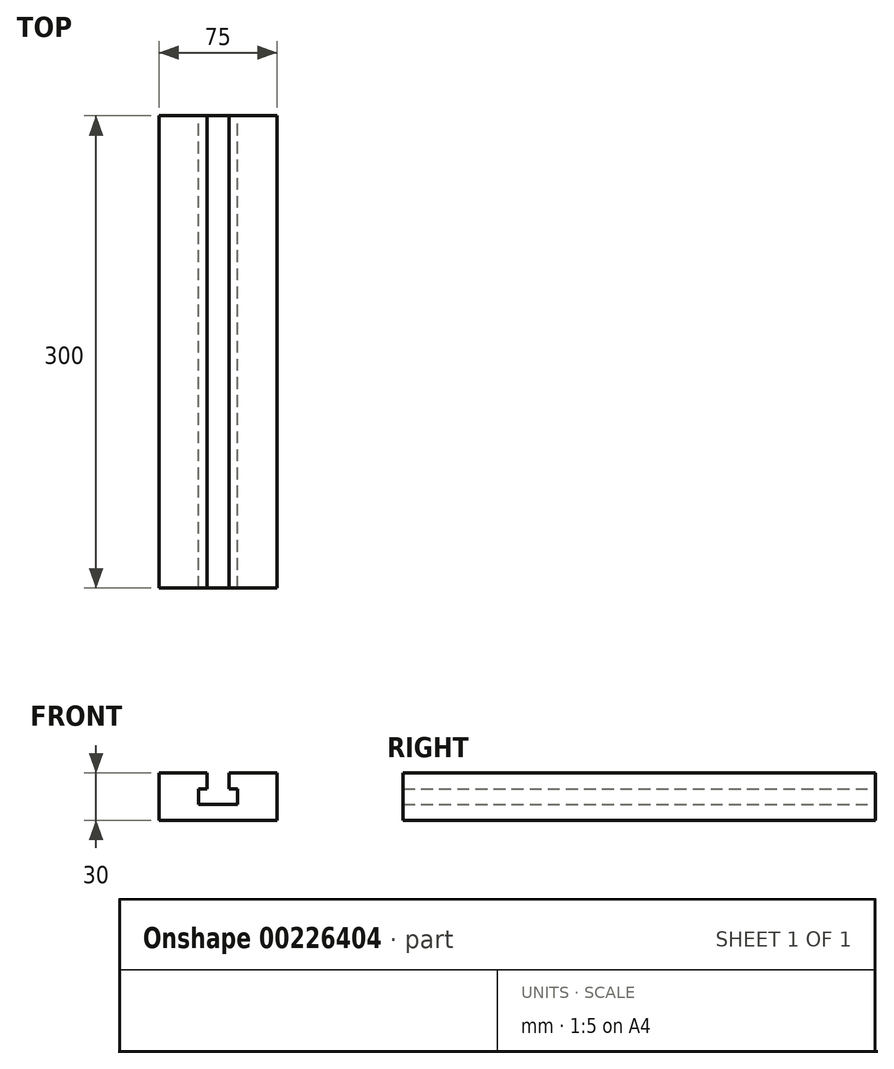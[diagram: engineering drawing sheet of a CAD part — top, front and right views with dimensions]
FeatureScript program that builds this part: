
annotation { "Feature Type Name" : "Feature", "Feature Type Description" : "" }
export const myFeature = defineFeature(function(context is Context, id is Id, definition is map)
    precondition{}
    {
        {
            var Q0;
            Q0=qCreatedBy(makeId("Front.planeOp"),FACE);
            var sketch = newSketch(context, id + "F0", { "sketchPlane" : qUnion([Q0])});
            skLineSegment(sketch, "E0.bottom", {"start": v(37.5, -15) * mm, "end": v(-37.5, -15) * mm});
            skLineSegment(sketch, "E0.top", {"start": v(37.5, 15) * mm, "end": v(-37.5, 15) * mm});
            skLineSegment(sketch, "E0.left", {"start": v(37.5, -15) * mm, "end": v(37.5, 15) * mm});
            skLineSegment(sketch, "E0.right", {"start": v(-37.5, -15) * mm, "end": v(-37.5, 15) * mm});
            skPoint(sketch, "E0.middle", {"position": v(0, 0) * mm});
            skLineSegment(sketch, "E1.bottom", {"start": v(7, 15) * mm, "end": v(-7, 15) * mm});
            skLineSegment(sketch, "E1.top", {"start": v(7, 5) * mm, "end": v(-7, 5) * mm});
            skLineSegment(sketch, "E1.left", {"start": v(7, 15) * mm, "end": v(7, 5) * mm});
            skLineSegment(sketch, "E1.right", {"start": v(-7, 15) * mm, "end": v(-7, 5) * mm});
            skPoint(sketch, "E1.middle", {"position": v(0, 10) * mm});
            skLineSegment(sketch, "E2.bottom", {"start": v(12.5, 5) * mm, "end": v(-12.5, 5) * mm});
            skLineSegment(sketch, "E2.top", {"start": v(12.5, -5) * mm, "end": v(-12.5, -5) * mm});
            skLineSegment(sketch, "E2.left", {"start": v(12.5, 5) * mm, "end": v(12.5, -5) * mm});
            skLineSegment(sketch, "E2.right", {"start": v(-12.5, 5) * mm, "end": v(-12.5, -5) * mm});
            skSolve(sketch);
        }
        {
            var Q0;
            Q0=makeQuery(id+"F0.imprint","IMPRINT",FACE,{"disambiguationData":[TD([[makeQuery(id+"F0.imprint","IMPRINT",EDGE,{"derivedFrom":sQuery(id+"F0.wireOp",EDGE,"E0.bottom")}),-1.0]])]});
            extrude(context, id + "F1", {"entities" : qUnion([Q0]), "depth" : 300 * mm});
        }
    });
